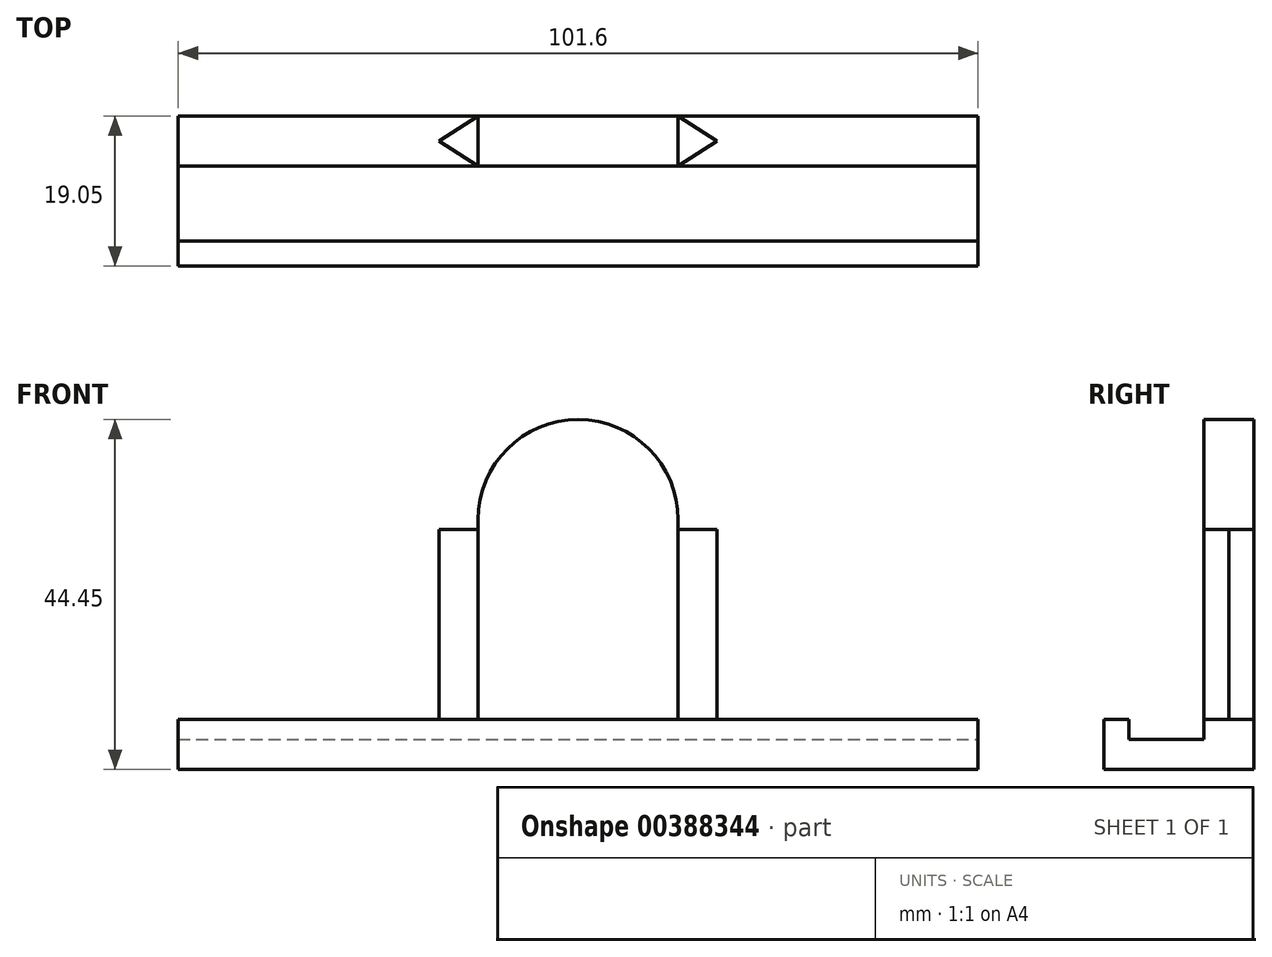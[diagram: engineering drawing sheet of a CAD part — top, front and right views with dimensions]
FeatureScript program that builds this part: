
annotation { "Feature Type Name" : "Feature", "Feature Type Description" : "" }
export const myFeature = defineFeature(function(context is Context, id is Id, definition is map)
    precondition{}
    {
        {
            var Q0;
            Q0=qCreatedBy(makeId("Front.planeOp"),FACE);
            var sketch = newSketch(context, id + "F0", { "sketchPlane" : qUnion([Q0])});
            skLineSegment(sketch, "E0.bottom", {"start": v(0, 0) * mm, "end": v(25.4, 0) * mm});
            skLineSegment(sketch, "E0.left", {"start": v(0, 0) * mm, "end": v(0, 25.4) * mm});
            skLineSegment(sketch, "E0.right", {"start": v(25.4, 0) * mm, "end": v(25.4, 25.4) * mm});
            skArc(sketch, "E1", {"start": v(25.4, 25.4) * mm, "mid": v(12.7, 38.1) * mm, "end": v(0, 25.4) * mm});
            skSolve(sketch);
        }
        {
            var Q0;
            Q0 = qSketchRegion(id + "F0", true);
            extrude(context, id + "F1", {"entities" : qUnion([Q0]), "depth" : 6.35 * mm});
        }
        {
            var Q0;
            Q0=makeQuery(id+"F1.opExtrude","SWEPT_FACE",FACE,{"disambiguationData":[OSD([sQuery(id+"F0.wireOp",EDGE,"E0.bottom")])]});
            var sketch = newSketch(context, id + "F2", { "sketchPlane" : qUnion([Q0])});
            skPoint(sketch, "E2.endSnap0", {"position": v(25.4, 3.18) * mm});
            skLineSegment(sketch, "E3", {"start": v(0, 0) * mm, "end": v(-4.95, 3.18) * mm});
            skLineSegment(sketch, "E4", {"start": v(0, 6.35) * mm, "end": v(-4.95, 3.18) * mm});
            skLineSegment(sketch, "E5", {"start": v(25.4, 6.35) * mm, "end": v(30.35, 3.18) * mm});
            skLineSegment(sketch, "E6", {"start": v(30.35, 3.18) * mm, "end": v(30.35, 3.18) * mm});
            skLineSegment(sketch, "E7", {"start": v(25.4, 0) * mm, "end": v(30.35, 3.18) * mm});
            skPoint(sketch, "E8.start.orphan", {"position": v(0, 3.18) * mm});
            skPoint(sketch, "E2.start.orphan", {"position": v(25.4, 3.18) * mm});
            skLineSegment(sketch, "E9", {"start": v(0, 0) * mm, "end": v(0, 6.35) * mm});
            skLineSegment(sketch, "E10", {"start": v(25.4, 6.35) * mm, "end": v(25.4, 0) * mm});
            skSolve(sketch);
        }
        {
            var Q0;
            Q0 = qSketchRegion(id + "F2", true);
            extrude(context, id + "F3", {"entities" : qUnion([Q0]), "operationType" : NewBodyOperationType.ADD, "oppositeDirection" : true, "depth" : 24.13 * mm});
        }
        {
            var Q0;
            Q0=makeQuery(id+"F3.boolean.opBoolean","MERGE",FACE,{"derivedFrom":[makeQuery(id+"F1.opExtrude","SWEPT_FACE",FACE,{"disambiguationData":[OSD([sQuery(id+"F0.wireOp",EDGE,"E0.bottom")])]}),makeQuery(id+"F3.opExtrude","CAP_FACE",FACE,{"disambiguationData":[OSD([sQuery(id+"F2.wireOp",EDGE,"E3"),sQuery(id+"F2.wireOp",EDGE,"E4"),sQuery(id+"F2.wireOp",EDGE,"E9")])],"isStart":true}),makeQuery(id+"F3.opExtrude","CAP_FACE",FACE,{"disambiguationData":[OSD([sQuery(id+"F2.wireOp",EDGE,"E5"),sQuery(id+"F2.wireOp",EDGE,"E7"),sQuery(id+"F2.wireOp",EDGE,"E10")])],"isStart":true})]});
            var sketch = newSketch(context, id + "F4", { "sketchPlane" : qUnion([Q0])});
            skLineSegment(sketch, "E11.bottom", {"start": v(63.5, 0) * mm, "end": v(-38.1, 0) * mm});
            skLineSegment(sketch, "E11.top", {"start": v(63.5, 6.35) * mm, "end": v(-38.1, 6.35) * mm});
            skLineSegment(sketch, "E11.left", {"start": v(63.5, 0) * mm, "end": v(63.5, 6.35) * mm});
            skLineSegment(sketch, "E11.right", {"start": v(-38.1, 0) * mm, "end": v(-38.1, 6.35) * mm});
            skSolve(sketch);
        }
        {
            var Q0;
            Q0 = qSketchRegion(id + "F4", true);
            extrude(context, id + "F5", {"entities" : qUnion([Q0]), "operationType" : NewBodyOperationType.ADD, "depth" : 6.35 * mm});
        }
        {
            var Q0;
            Q0=makeQuery(id+"F5.boolean.opBoolean","MERGE",FACE,{"derivedFrom":[makeQuery(id+"F1.opExtrude","CAP_FACE",FACE,{"disambiguationData":[OSD([sQuery(id+"F0.wireOp",EDGE,"E0.bottom"),sQuery(id+"F0.wireOp",EDGE,"E0.left"),sQuery(id+"F0.wireOp",EDGE,"E0.right"),sQuery(id+"F0.wireOp",EDGE,"E1")])],"isStart":false}),makeQuery(id+"F5.opExtrude","SWEPT_FACE",FACE,{"disambiguationData":[OSD([sQuery(id+"F4.wireOp",EDGE,"E11.top")])]})]});
            var sketch = newSketch(context, id + "F6", { "sketchPlane" : qUnion([Q0])});
            skLineSegment(sketch, "E12", {"start": v(0, 0) * mm, "end": v(25.4, 0) * mm});
            skSolve(sketch);
        }
        {
            var Q0;
            Q0 = qSketchRegion(id + "F6", true);
            var Q1;
            Q1=makeQuery(id+"F6.imprint","IMPRINT",FACE,{"disambiguationData":[TD([[makeQuery(id+"F6.imprint","IMPRINT",EDGE,{"derivedFrom":sQuery(id+"F6.wireOp",EDGE,"E12")}),-1.0]])]});
            extrude(context, id + "F7", {"entities" : qUnion([Q0, Q1]), "operationType" : NewBodyOperationType.ADD, "depth" : 12.7 * mm});
        }
        {
            var Q0;
            {var subQ0=sQuery(id+"F4.wireOp",EDGE,"E11.left");Q0=makeQuery(id+"F7.boolean.opBoolean","MERGE",FACE,{"derivedFrom":[makeQuery(id+"F5.opExtrude","SWEPT_FACE",FACE,{"disambiguationData":[OSD([subQ0])]}),makeQuery(id+"F7.opExtrude","SWEPT_FACE",FACE,{"disambiguationData":[OSD([sQuery(id+"F4.wireOp",EDGE,"E11.top"),subQ0])]})]});}
            var sketch = newSketch(context, id + "F8", { "sketchPlane" : qUnion([Q0])});
            skLineSegment(sketch, "E13.bottom", {"start": v(-15.87, 0) * mm, "end": v(-6.35, 0) * mm});
            skLineSegment(sketch, "E13.top", {"start": v(-15.87, -2.54) * mm, "end": v(-6.35, -2.54) * mm});
            skLineSegment(sketch, "E13.left", {"start": v(-15.87, 0) * mm, "end": v(-15.87, -2.54) * mm});
            skLineSegment(sketch, "E13.right", {"start": v(-6.35, 0) * mm, "end": v(-6.35, -2.54) * mm});
            skSolve(sketch);
        }
        {
            var Q0;
            Q0 = qSketchRegion(id + "F8", true);
            extrude(context, id + "F9", {"entities" : qUnion([Q0]), "operationType" : NewBodyOperationType.REMOVE, "oppositeDirection" : true, "depth" : 114.28 * mm});
        }
    });
